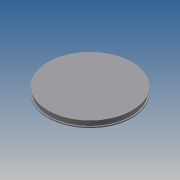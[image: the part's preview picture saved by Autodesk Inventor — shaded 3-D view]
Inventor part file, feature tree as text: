
AUTODESK INVENTOR PART (.ipt)
format: ipt  version: 2013 (Build 170138000, 138)  size: 91,136 bytes
history: native  units: mm
features: extrude x4, sketch x4
ambient origin geometry x8: Origin, YZ Plane, XZ Plane, XY Plane, X Axis, Y Axis, Z Axis, Center Point
bodies: Solid1 (feature_tree)
feature tree (8):
  extrude  "Extrusion1"  Depth=2.0mm TaperAngle=0.0deg
  extrude  "Extrusion2"  Depth=8.0mm TaperAngle=0.0deg
  extrude  "Extrusion3"  Depth=12.5mm
  extrude  "Extrusion4"  [1 undecoded]
  sketch  "Sketch1"  dims[d0=154.0mm d2=2.0mm d3=0.0mm]
  sketch  "Sketch2"  dims[d4=150.0mm d6=8.0mm d7=0.0mm]
  sketch  "Sketch3"  dims[d8=2.0mm d9=0.0mm d10=12.5mm]
  sketch  "Sketch4"  dims[d12=2.0mm d13=0.0mm]
note: 1 required parameter value undecoded (feature->parameter linkage not recoverable at this tier; creation-order binding heuristic only, values carry confidence <= 0.55)
